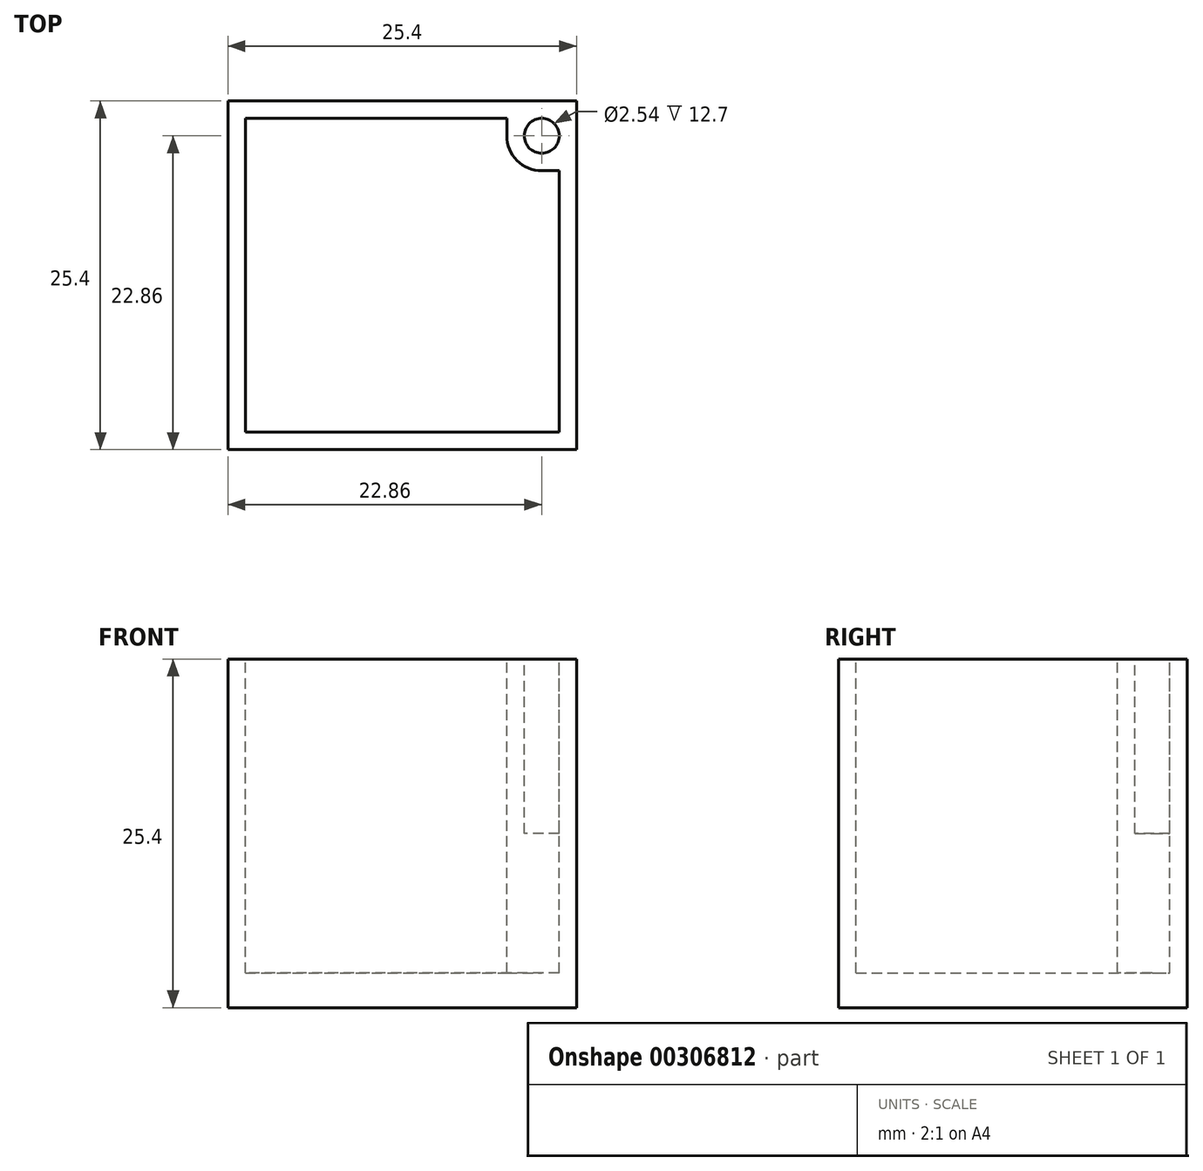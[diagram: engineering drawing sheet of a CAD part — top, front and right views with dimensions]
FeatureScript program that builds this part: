
annotation { "Feature Type Name" : "Feature", "Feature Type Description" : "" }
export const myFeature = defineFeature(function(context is Context, id is Id, definition is map)
    precondition{}
    {
        {
            var Q0;
            Q0=qCreatedBy(makeId("Top.planeOp"),FACE);
            var sketch = newSketch(context, id + "F0", { "sketchPlane" : qUnion([Q0])});
            skLineSegment(sketch, "E0", {"start": v(0, 0) * mm, "end": v(0, 25.4) * mm});
            skLineSegment(sketch, "E1", {"start": v(0, 25.4) * mm, "end": v(25.4, 25.4) * mm});
            skLineSegment(sketch, "E2", {"start": v(25.4, 25.4) * mm, "end": v(25.4, 0) * mm});
            skLineSegment(sketch, "E3", {"start": v(25.4, 0) * mm, "end": v(0, 0) * mm});
            skSolve(sketch);
        }
        {
            var Q0;
            Q0=makeQuery(id+"F0.imprint","IMPRINT",FACE,{"disambiguationData":[TD([[makeQuery(id+"F0.imprint","IMPRINT",EDGE,{"derivedFrom":sQuery(id+"F0.wireOp",EDGE,"E0")}),-1.0]])]});
            extrude(context, id + "F1", {"entities" : qUnion([Q0]), "depth" : 25.4 * mm});
        }
        {
            var Q0;
            Q0=makeQuery(id+"F1.opExtrude","CAP_FACE",FACE,{"disambiguationData":[OSD([sQuery(id+"F0.wireOp",EDGE,"E0"),sQuery(id+"F0.wireOp",EDGE,"E1"),sQuery(id+"F0.wireOp",EDGE,"E2"),sQuery(id+"F0.wireOp",EDGE,"E3")])],"isStart":false});
            var sketch = newSketch(context, id + "F2", { "sketchPlane" : qUnion([Q0])});
            skCircle(sketch, "E4", {"center": v(22.86, 22.86) * mm, "radius": 1.27 * mm});
            skSolve(sketch);
        }
        {
            var Q0;
            Q0=makeQuery(id+"F2.imprint","IMPRINT",FACE,{"disambiguationData":[TD([[makeQuery(id+"F2.imprint","IMPRINT",EDGE,{"derivedFrom":sQuery(id+"F2.wireOp",EDGE,"E4")}),1.0]])]});
            extrude(context, id + "F3", {"entities" : qUnion([Q0]), "operationType" : NewBodyOperationType.REMOVE, "oppositeDirection" : true, "depth" : 12.7 * mm});
        }
        {
            var Q0;
            Q0=makeQuery(id+"F1.opExtrude","CAP_FACE",FACE,{"disambiguationData":[OSD([sQuery(id+"F0.wireOp",EDGE,"E0"),sQuery(id+"F0.wireOp",EDGE,"E1"),sQuery(id+"F0.wireOp",EDGE,"E2"),sQuery(id+"F0.wireOp",EDGE,"E3")])],"isStart":false});
            var sketch = newSketch(context, id + "F4", { "sketchPlane" : qUnion([Q0])});
            skLineSegment(sketch, "E5", {"start": v(25.4, 25.4) * mm, "end": v(25.4, 20.32) * mm});
            skLineSegment(sketch, "E6", {"start": v(25.4, 20.32) * mm, "end": v(20.32, 20.32) * mm});
            skLineSegment(sketch, "E7", {"start": v(20.32, 20.32) * mm, "end": v(20.32, 25.4) * mm});
            skLineSegment(sketch, "E8", {"start": v(1.27, 24.13) * mm, "end": v(20.32, 24.13) * mm});
            skLineSegment(sketch, "E9", {"start": v(1.27, 1.27) * mm, "end": v(1.27, 24.13) * mm});
            skLineSegment(sketch, "E10", {"start": v(24.13, 1.27) * mm, "end": v(1.27, 1.27) * mm});
            skLineSegment(sketch, "E11", {"start": v(24.13, 1.27) * mm, "end": v(24.13, 20.32) * mm});
            skSolve(sketch);
        }
        {
            var Q0;
            {var subQ0=sQuery(id+"F4.wireOp",EDGE,"E8");Q0=makeQuery(id+"F4.imprint","IMPRINT",FACE,{"disambiguationData":[TD([[makeQuery(id+"F4.imprint","IMPRINT",EDGE,{"derivedFrom":subQ0}),-1.0]])]});}
            extrude(context, id + "F5", {"entities" : qUnion([Q0]), "operationType" : NewBodyOperationType.REMOVE, "oppositeDirection" : true, "depth" : 22.86 * mm});
        }
        {
            var Q0;
            Q0=makeQuery(id+"F5.boolean.opBoolean","COPY",EDGE,{"derivedFrom":makeQuery(id+"F5.opExtrude","SWEPT_EDGE",EDGE,{"disambiguationData":[OSD([sQuery(id+"F4.wireOp",EDGE,"E6"),sQuery(id+"F4.wireOp",EDGE,"E7")])]})});
            fillet(context, id + "F6", {"entities" : qUnion([Q0]), "radius" : 2.54 * mm, "tangentPropagation" : true, "allowEdgeOverflow" : false});
        }
    });
